# Revit family: Haworth_BuzziFloat_Chair
name_source: partatom
category: Furniture
revit_build: Autodesk Revit 2018 (Build: 20170223_1515(x64)
units: mm (PartAtom-declared; Revit-internal decimal feet)

## family parameters
Always vertical = Yes
Cut with Voids When Loaded = No
OmniClass Number = 23.40.20.00
OmniClass Title = General Furniture and Specialties
Room Calculation Point = No
Shared = No
Work Plane-Based = No

## types (3) — shared parameters
Actual Depth = 20.08 "
Actual Height = 31.1 "
Actual Width = 22.83 "
Assembly Code = E2020200
Glide Finish = Haworth _ Polymer _ Slate
Hardware Finish = Haworth _ Metal _ Chrome
Manufacturer = Haworth
Model = HCBZ-FL
Revision = 1
Seat Height = 18.5 "
Size = Verify Final Dim. w/ Haworth
URL = http://www.haworth.com
URL - Product = https://www.haworth.com
Warranty = http://www.haworth.com

## per-type parameters (varying)
| type | Description | Four Angled Legs | Four Caster Base | Four Legs |
| HCBZ-FLS4 - Side Chair | Haworth BuzziFloat Side Chair - Four Legs | No | No | Yes |
| HCBZ-FLSA - Side Chair with Angled Legs | Haworth BuzziFloat Side Chair - Four Angled Legs | Yes | No | No |
| HCBZ-FLC4 - Conference Chair | Haworth BuzziFloat Conference Chair | No | Yes | No |

## geometry (parser evidence)
native form markers: Sweep x5
no freeform markers — native parametric forms only
